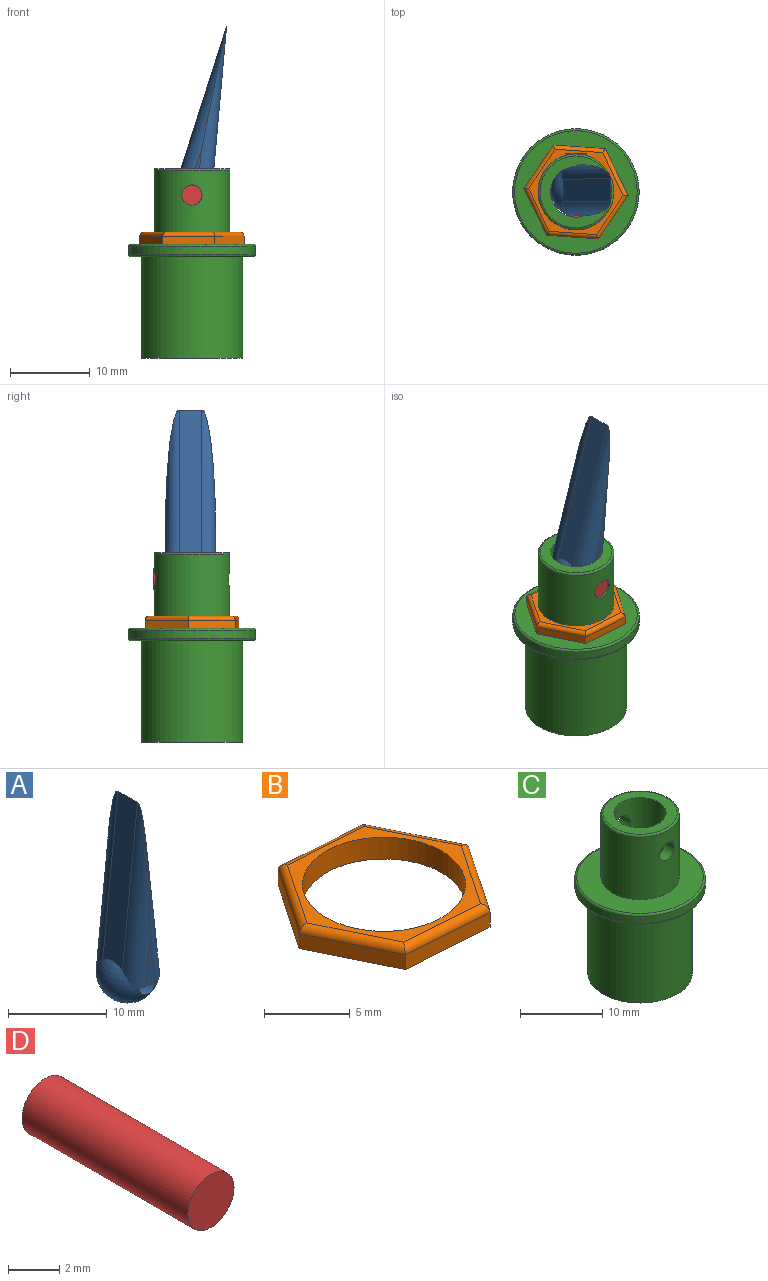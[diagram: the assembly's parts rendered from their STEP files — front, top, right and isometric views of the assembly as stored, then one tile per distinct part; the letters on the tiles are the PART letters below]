
ASSEMBLY  parts=4 mates=3
PART A: 11 faces, bbox 6.4x6.4x24.9 mm
  f0: sphere r=3.17mm, area 78.4mm2, adj f1,f2,f3,f4,f7,f8,f9,f10
  f1: cylinder r=1.27mm len=5.82mm, axis (0,-1,0), area 23.5mm2, adj f0,f2
  f2: plane 6.38x4.26mm, normal (-0.01,0,-1), area 16.4mm2, adj f0,f1,f5,f6,f7,f8,f9,f10
  f3: plane 19.93x2.79mm, normal (0.99,0,0.11), area 55mm2, adj f0,f4,f8,f10
  f4: plane 19.8x2.79mm, normal (-0.99,0,0.11), area 54.6mm2, adj f0,f3,f7,f9
  f5: plane 5.56x1.24mm, normal (0,-1,0), area 3.4mm2, adj f2,f9,f10
  f6: plane 5.56x1.24mm, normal (0,1,0), area 3.4mm2, adj f2,f7,f8
  f7: cylinder r=1.78mm len=21.77mm, axis (-0.11,0,-0.99), area 42.9mm2, adj f0,f2,f4,f6,f8
  f8: cylinder r=1.78mm len=21.83mm, axis (-0.11,0,0.99), area 43.3mm2, adj f0,f2,f3,f6,f7
  f9: cylinder r=1.78mm len=21.77mm, axis (0.11,0,0.99), area 42.9mm2, adj f0,f2,f4,f5,f10
  f10: cylinder r=1.78mm len=21.83mm, axis (0.11,0,-0.99), area 43.3mm2, adj f0,f2,f3,f5,f9
PART B: 15 faces, bbox 13.1x11.8x1.6 mm
  f0: plane 5.89x2.87mm, normal (0.9,0.44,0), area 6.9mm2, adj f1,f6,f8,f10
  f1: plane 6.53x1.05mm, normal (0.07,1,0), area 6.9mm2, adj f0,f2,f8,f9
  f2: plane 5.43x3.67mm, normal (-0.83,0.56,0), area 6.9mm2, adj f1,f3,f8,f11
  f3: plane 5.89x2.87mm, normal (-0.9,-0.44,0), area 6.9mm2, adj f2,f4,f8,f13
  f4: plane 6.53x1.05mm, normal (-0.07,-1,0), area 6.9mm2, adj f3,f6,f8,f14
  f5: cylinder r=4.76mm len=9.53mm, axis (0,0,-1), area 46.6mm2, adj f7,f8
  f6: plane 5.43x3.67mm, normal (0.83,-0.56,0), area 6.9mm2, adj f0,f4,f8,f12
  f7: plane 11.9x10.72mm, normal (0,0,1), area 21.1mm2, adj f5,f9,f10,f11,f12,f13,f14
  f8: plane 13.07x11.78mm, normal (0,0,-1), area 40.2mm2, adj f0,f1,f2,f3,f4,f5,f6
  f9: cylinder r=0.51mm len=6.57mm, axis (1,-0.07,0), area 5.1mm2, adj f1,f7,f10,f11
  f10: cylinder r=0.51mm len=6.11mm, axis (0.44,-0.9,0), area 5.1mm2, adj f0,f7,f9,f12
  f11: cylinder r=0.51mm len=5.71mm, axis (0.56,0.83,0), area 5.1mm2, adj f2,f7,f9,f13
  f12: cylinder r=0.51mm len=5.71mm, axis (-0.56,-0.83,0), area 5.1mm2, adj f6,f7,f10,f14
  f13: cylinder r=0.51mm len=6.11mm, axis (-0.44,0.9,0), area 5.1mm2, adj f3,f7,f11,f14
  f14: cylinder r=0.51mm len=6.57mm, axis (-1,0.07,0), area 5.1mm2, adj f4,f7,f12,f13
PART C: 13 faces, bbox 17.2x17.2x23.8 mm
  f0: cylinder r=1.27mm len=2.54mm, axis (0,1,0), area 13mm2, adj f1,f12
  f1: cylinder r=4.76mm len=9.53mm, axis (0,0,-1), area 267.2mm2, adj f0,f5,f8,f11
  f2: cylinder r=6.35mm len=12.7mm, axis (0,0,1), area 506.7mm2, adj f3,f6
  f3: plane 12.7x12.7mm, normal (0,0,-1), area 95mm2, adj f2,f12
  f4: cylinder r=7.94mm len=15.88mm, axis (0,0,-1), area 52.3mm2, adj f9,f10
  f5: plane 15.37x15.37mm, normal (0,0,1), area 114.2mm2, adj f1,f10
  f6: plane 15.37x15.37mm, normal (0,0,-1), area 58.8mm2, adj f2,f9
  f7: plane 9.02x9.02mm, normal (0,0,1), area 32.2mm2, adj f8,f12
  f8: torus R=4.51mm, axis (0,0,1), area 11.7mm2, adj f1,f7
  f9: torus R=7.68mm, axis (0,0,1), area 19.7mm2, adj f4,f6
  f10: torus R=7.68mm, axis (0,0,1), area 19.7mm2, adj f4,f5
  f11: cylinder r=1.27mm len=2.54mm, axis (0,1,0), area 13mm2, adj f1,f12
  f12: cylinder r=3.17mm len=23.78mm, axis (0,0,1), area 464mm2, adj f0,f3,f7,f11
PART D: 3 faces, bbox 2.5x9.1x2.5 mm
  f0: cylinder r=1.27mm len=9.14mm, axis (0,1,0), area 73mm2, adj f1,f2
  f1: plane 2.54x2.54mm, normal (0,-1,0), area 5.1mm2, adj f0
  f2: plane 2.54x2.54mm, normal (0,1,0), area 5.1mm2, adj f0
PLACE A rot(axis=(0,1,0),11.6deg) t=(12.97,1.85,-0.2)mm
PLACE B t=(12.97,1.65,-6.39)mm
PLACE C t=(12.97,1.65,-7.95)mm fixed
PLACE D t=(12.97,6.42,-0.2)mm
MATE revolute A.f1 <-> D.f0  axis (0,-1,0) through (12.97,1.85,-0.2)mm
MATE fastened B.f5 <-> C.f1  axis (0,0,-1) through (12.97,1.65,-6.39)mm
MATE fastened D.f0 <-> C.f0  axis (0,1,0) through (12.97,6.42,-0.2)mm
